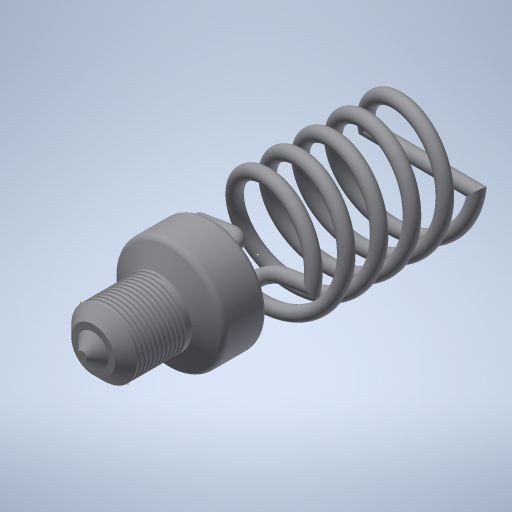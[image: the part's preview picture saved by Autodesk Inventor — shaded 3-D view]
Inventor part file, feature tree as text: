
AUTODESK INVENTOR PART (.ipt)
format: ipt  version: 2024 (Build 280153000, 153)  size: 956,416 bytes
history: native  units: mm
features: sketch x9, plane x3, other x3, sweep x2, extrude x2, revolve x1, fillet x1, chamfer x1
ambient origin geometry x8: Origin, YZ Plane, XZ Plane, XY Plane, X Axis, Y Axis, Z Axis, Center Point
bodies: Solid1 (feature_tree)
feature tree (22):
  revolve  "Revolution1"  [1 undecoded]
  fillet  "Fillet1"  Radius=20.0mm
  chamfer  "Chamfer1"  Distance=3.0mm
  plane  "Work Plane1"
  sketch  "Sketch2"  dims[d3=30.0mm]
  sweep  "Sweep1"
  plane  "Work Plane2"
  sketch  "Sketch4"  dims[d5=45.0deg]
  sketch  "3D Sketch2"
  plane  "Work Plane3"
  sweep  "Sweep2"
  extrude  "Extrusion1"  Depth=30.0mm TaperAngle=0.0deg
  extrude  "Extrusion2"  Depth=30.0mm TaperAngle=0.0deg
  sketch  "Sketch1"  dims[d0=60.0mm d1=25.0mm d2=20.0mm]
  sketch  "3D Sketch1"
  other  "Helical Curve1"
  other  "Helical Curve2"
  sketch  "Sketch3"  dims[d4=2.0mm]
  other  "Helical Curve3"
  sketch  "Sketch6"  dims[d6=15.0mm]
  sketch  "Sketch7"  dims[d7=5.0mm]
  sketch  "Sketch8"  dims[d8=90.0deg d9=3.0mm d10=5.0mm d11=2.0mm d12=45.0deg d13=20.0mm d14=30.0mm d15=25.0mm d16=50.0mm d17=0.0mm d18=30.0mm d19=25.0mm d20=50.0mm d21=0.0mm d28=7.0mm d29=7.0mm d30=20.0mm d31=20.0mm d32=6.0mm d33=6.0mm d34=3.0mm d35=0.0mm d36=-5.0mm d37=0.0mm d38=2.0mm d39=115.0mm d40=30.0mm d41=0.0mm d42=1.5mm d43=0.0mm d44=0.0mm d45=1.5mm d46=0.0mm d47=0.0mm d48=1.5mm d49=0.0mm d50=0.0mm]
note: 1 required parameter value undecoded (feature->parameter linkage not recoverable at this tier; creation-order binding heuristic only, values carry confidence <= 0.55)
